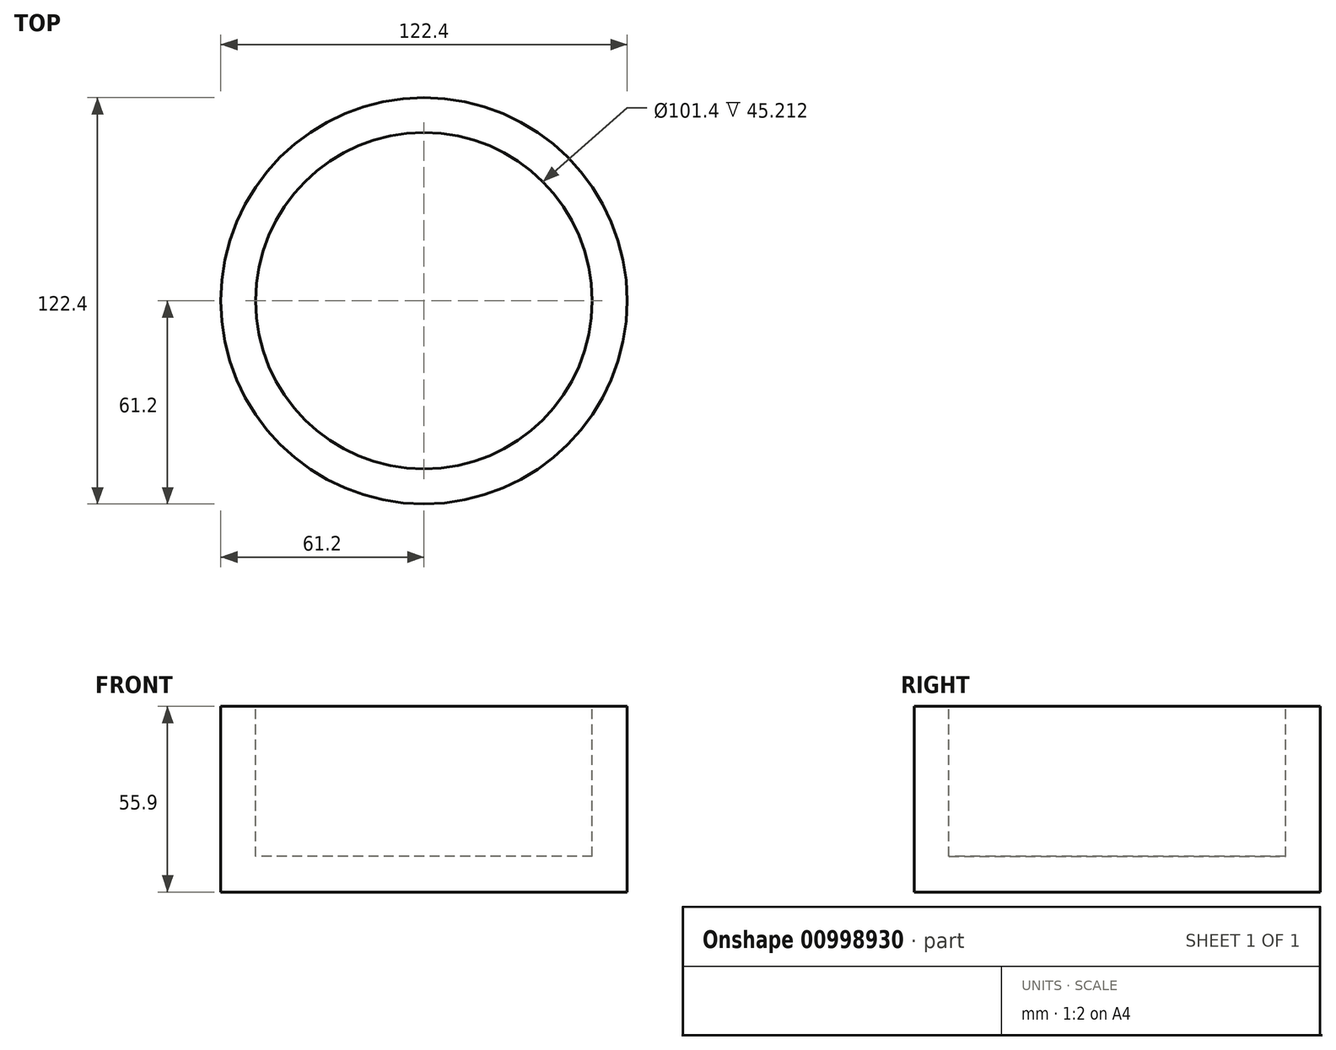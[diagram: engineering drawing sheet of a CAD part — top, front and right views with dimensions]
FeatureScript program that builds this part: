
annotation { "Feature Type Name" : "Feature", "Feature Type Description" : "" }
export const myFeature = defineFeature(function(context is Context, id is Id, definition is map)
    precondition{}
    {
        {
            var Q0;
            Q0=qCreatedBy(makeId("Front.planeOp"),FACE);
            var sketch = newSketch(context, id + "F0", { "sketchPlane" : qUnion([Q0])});
            skLineSegment(sketch, "E0.bottom", {"start": v(0, 0) * mm, "end": v(61.2, 0) * mm});
            skLineSegment(sketch, "E0.top", {"start": v(0, 55.9) * mm, "end": v(61.2, 55.9) * mm});
            skLineSegment(sketch, "E0.left", {"start": v(0, 0) * mm, "end": v(0, 55.9) * mm});
            skLineSegment(sketch, "E0.right", {"start": v(61.2, 0) * mm, "end": v(61.2, 55.9) * mm});
            skLineSegment(sketch, "E1.bottom", {"start": v(0, 0) * mm, "end": v(0, 0) * mm});
            skLineSegment(sketch, "E1.top", {"start": v(0, 89.43) * mm, "end": v(0, 89.43) * mm});
            skLineSegment(sketch, "E1.left", {"start": v(0, 0) * mm, "end": v(0, 89.43) * mm, "construction": true});
            skLineSegment(sketch, "E1.right", {"start": v(0, 0) * mm, "end": v(0, 89.43) * mm, "construction": true});
            skSolve(sketch);
        }
        {
            var Q0;
            Q0 = qSketchRegion(id + "F0", true);
            var Q1;
            Q1=sQuery(id+"F0.wireOp",EDGE,"E1.right");
            revolve(context, id + "F1", {"surfaceOperationType" : NewSurfaceOperationType.NEW, "entities" : qUnion([Q0]), "axis" : qUnion([Q1]), "revolveType" : RevolveType.FULL});
        }
        {
            var Q0;
            Q0=makeQuery(id+"F1.opRevolve","SWEPT_FACE",FACE,{"disambiguationData":[OSD([sQuery(id+"F0.wireOp",EDGE,"E0.top")])]});
            var sketch = newSketch(context, id + "F2", { "sketchPlane" : qUnion([Q0])});
            skCircle(sketch, "E2", {"center": v(0, 0) * mm, "radius": 50.7 * mm});
            skSolve(sketch);
        }
        {
            var Q0;
            Q0=makeQuery(id+"F2.imprint","IMPRINT",FACE,{"disambiguationData":[TD([[makeQuery(id+"F2.imprint","IMPRINT",EDGE,{"derivedFrom":sQuery(id+"F2.wireOp",EDGE,"E2")}),1.0]])]});
            extrude(context, id + "F3", {"entities" : qUnion([Q0]), "operationType" : NewBodyOperationType.REMOVE, "oppositeDirection" : true, "depth" : 45.2 * mm, "offsetDistance" : 25.4 * mm});
        }
    });
